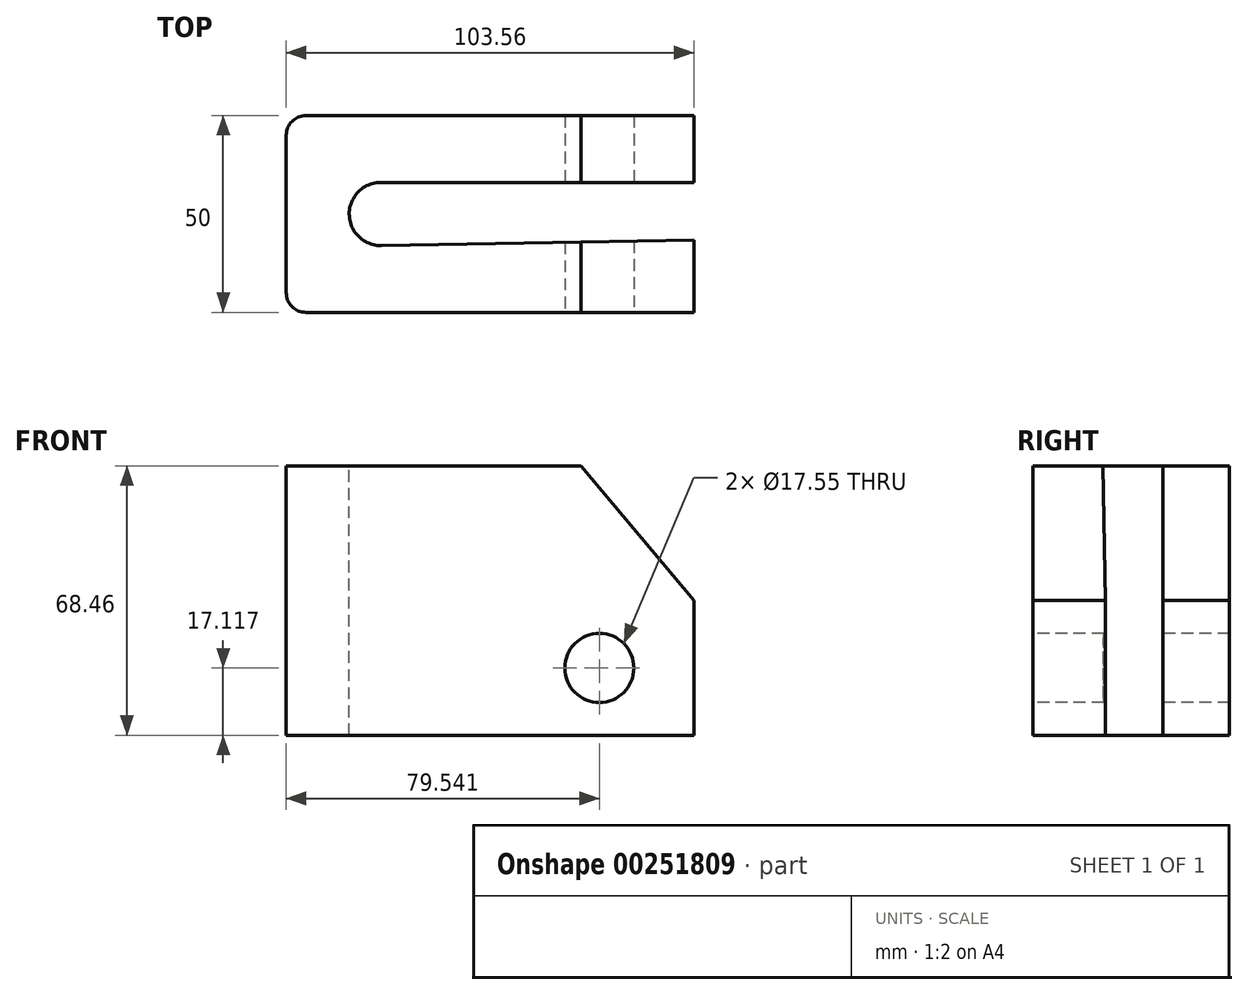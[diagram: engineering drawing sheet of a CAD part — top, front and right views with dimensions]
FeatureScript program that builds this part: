
annotation { "Feature Type Name" : "Feature", "Feature Type Description" : "" }
export const myFeature = defineFeature(function(context is Context, id is Id, definition is map)
    precondition{}
    {
        {
            var Q0;
            Q0=qCreatedBy(makeId("Front.planeOp"),FACE);
            var sketch = newSketch(context, id + "F0", { "sketchPlane" : qUnion([Q0])});
            skLineSegment(sketch, "E0.bottom", {"start": v(-51.78, 34.23) * mm, "end": v(51.78, 34.23) * mm});
            skLineSegment(sketch, "E0.top", {"start": v(-51.78, -34.23) * mm, "end": v(51.78, -34.23) * mm});
            skLineSegment(sketch, "E0.left", {"start": v(-51.78, 34.23) * mm, "end": v(-51.78, -34.23) * mm});
            skLineSegment(sketch, "E0.right", {"start": v(51.78, 34.23) * mm, "end": v(51.78, -34.23) * mm});
            skPoint(sketch, "E0.middle", {"position": v(0, 0) * mm});
            skSolve(sketch);
        }
        {
            var Q0;
            Q0 = qSketchRegion(id + "F0", true);
            extrude(context, id + "F1", {"entities" : qUnion([Q0]), "oppositeDirection" : true, "depth" : 50 * mm});
        }
        {
            var Q0;
            Q0=makeQuery(id+"F1.opExtrude","SWEPT_FACE",FACE,{"disambiguationData":[OSD([sQuery(id+"F0.wireOp",EDGE,"E0.bottom")])]});
            var sketch = newSketch(context, id + "F2", { "sketchPlane" : qUnion([Q0])});
            skCircle(sketch, "E1", {"center": v(-27.76, 25) * mm, "radius": 8.02 * mm});
            skPoint(sketch, "E1.centerSnap0", {"position": v(-51.78, 25) * mm});
            skSolve(sketch);
        }
        {
            var Q0;
            Q0 = qSketchRegion(id + "F2", true);
            var Q1;
            Q1=makeQuery(id+"F2.imprint","IMPRINT",FACE,{"disambiguationData":[TD([[makeQuery(id+"F2.imprint","IMPRINT",EDGE,{"derivedFrom":sQuery(id+"F2.wireOp",EDGE,"E1")}),1.0]])]});
            extrude(context, id + "F3", {"entities" : qUnion([Q0, Q1]), "operationType" : NewBodyOperationType.REMOVE, "oppositeDirection" : true, "depth" : 70 * mm});
        }
        {
            var Q0;
            Q0=makeQuery(id+"F1.opExtrude","SWEPT_FACE",FACE,{"disambiguationData":[OSD([sQuery(id+"F0.wireOp",EDGE,"E0.bottom")])]});
            var sketch = newSketch(context, id + "F4", { "sketchPlane" : qUnion([Q0])});
            skLineSegment(sketch, "E2", {"start": v(-27.76, 33.02) * mm, "end": v(51.78, 33.02) * mm});
            skLineSegment(sketch, "E3", {"start": v(-27.62, 16.99) * mm, "end": v(51.78, 18.4) * mm});
            skSolve(sketch);
        }
        {
            var Q0;
            Q0 = qSketchRegion(id + "F4", true);
            var Q1;
            {var subQ0=sQuery(id+"F4.wireOp",EDGE,"E2");Q1=makeQuery(id+"F4.imprint","IMPRINT",FACE,{"disambiguationData":[TD([[makeQuery(id+"F4.imprint","IMPRINT",EDGE,{"derivedFrom":subQ0}),-1.0]])]});}
            extrude(context, id + "F5", {"entities" : qUnion([Q0, Q1]), "operationType" : NewBodyOperationType.REMOVE, "oppositeDirection" : true, "depth" : 75 * mm});
        }
        {
            var Q0;
            Q0=makeQuery(id+"F1.opExtrude","CAP_FACE",FACE,{"disambiguationData":[OSD([sQuery(id+"F0.wireOp",EDGE,"E0.bottom"),sQuery(id+"F0.wireOp",EDGE,"E0.top"),sQuery(id+"F0.wireOp",EDGE,"E0.left"),sQuery(id+"F0.wireOp",EDGE,"E0.right")])],"isStart":true});
            var sketch = newSketch(context, id + "F6", { "sketchPlane" : qUnion([Q0])});
            skLineSegment(sketch, "E4", {"start": v(23.06, 34.23) * mm, "end": v(51.78, 0) * mm});
            skSolve(sketch);
        }
        {
            var Q0;
            {var subQ0=sQuery(id+"F6.wireOp",EDGE,"E4");Q0=makeQuery(id+"F6.imprint","IMPRINT",FACE,{"disambiguationData":[TD([[makeQuery(id+"F6.imprint","IMPRINT",EDGE,{"derivedFrom":subQ0}),1.0]])]});}
            extrude(context, id + "F7", {"entities" : qUnion([Q0]), "operationType" : NewBodyOperationType.REMOVE, "oppositeDirection" : true, "depth" : 60 * mm});
        }
        {
            var Q0;
            Q0=makeQuery(id+"F1.opExtrude","CAP_FACE",FACE,{"disambiguationData":[OSD([sQuery(id+"F0.wireOp",EDGE,"E0.bottom"),sQuery(id+"F0.wireOp",EDGE,"E0.top"),sQuery(id+"F0.wireOp",EDGE,"E0.left"),sQuery(id+"F0.wireOp",EDGE,"E0.right")])],"isStart":true});
            var sketch = newSketch(context, id + "F8", { "sketchPlane" : qUnion([Q0])});
            skCircle(sketch, "E5", {"center": v(27.76, -17.11) * mm, "radius": 8.78 * mm});
            skPoint(sketch, "E5.centerSnap0", {"position": v(51.78, -17.11) * mm});
            skSolve(sketch);
        }
        {
            var Q0;
            Q0 = qSketchRegion(id + "F8", true);
            extrude(context, id + "F9", {"entities" : qUnion([Q0]), "operationType" : NewBodyOperationType.REMOVE, "oppositeDirection" : true, "depth" : 75 * mm});
        }
        {
            var Q0;
            Q0=makeQuery(id+"F1.opExtrude","CAP_EDGE",EDGE,{"disambiguationData":[OSD([sQuery(id+"F0.wireOp",EDGE,"E0.left")])],"isStart":true});
            var Q1;
            Q1=makeQuery(id+"F1.opExtrude","CAP_EDGE",EDGE,{"disambiguationData":[OSD([sQuery(id+"F0.wireOp",EDGE,"E0.left")])],"isStart":false});
            fillet(context, id + "F10", {"entities" : qUnion([Q0, Q1]), "radius" : 5 * mm, "tangentPropagation" : true, "allowEdgeOverflow" : false});
        }
    });
